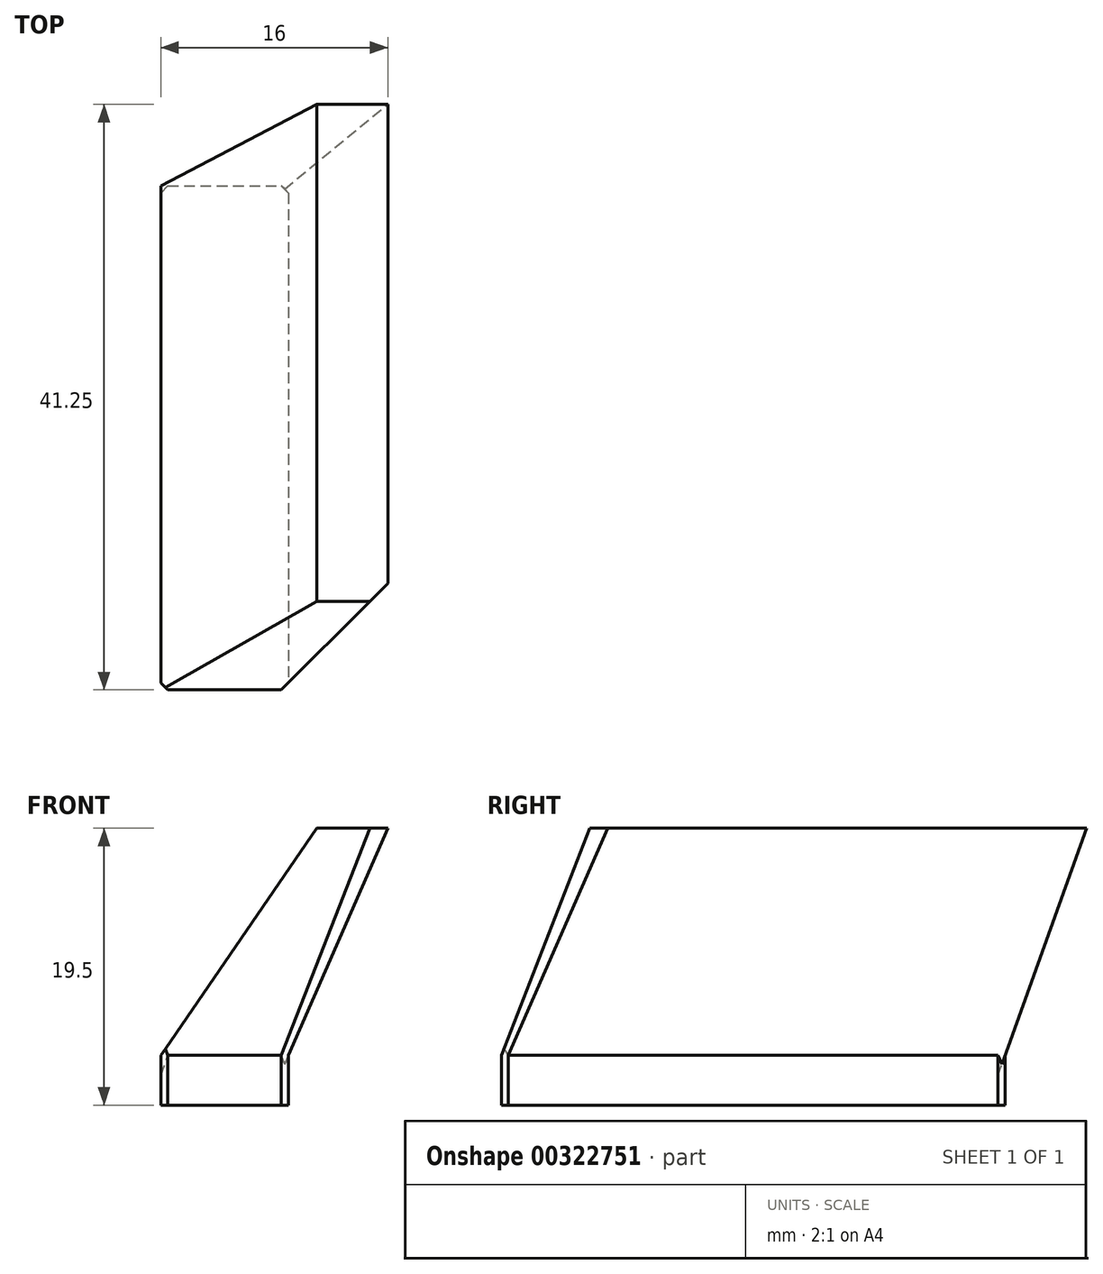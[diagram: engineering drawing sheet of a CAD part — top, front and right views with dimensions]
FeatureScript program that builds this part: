
annotation { "Feature Type Name" : "Feature", "Feature Type Description" : "" }
export const myFeature = defineFeature(function(context is Context, id is Id, definition is map)
    precondition{}
    {
        {
            assignVariable(context, id + "F0", {"variableType" : VariableType.LENGTH, "name" : "zoff", "lengthValue" : 16 * mm});
        }
        {
            var Q0;
            Q0=qCreatedBy(makeId("Top.planeOp"),FACE);
            var sketch = newSketch(context, id + "F1", { "sketchPlane" : qUnion([Q0])});
            skLineSegment(sketch, "E0.bottom", {"start": v(4.5, 17.75) * mm, "end": v(-4.5, 17.75) * mm});
            skLineSegment(sketch, "E0.top", {"start": v(4.5, -17.75) * mm, "end": v(-4.5, -17.75) * mm});
            skLineSegment(sketch, "E0.left", {"start": v(4.5, 17.75) * mm, "end": v(4.5, -17.75) * mm});
            skLineSegment(sketch, "E0.right", {"start": v(-4.5, 17.75) * mm, "end": v(-4.5, -17.75) * mm});
            skPoint(sketch, "E0.middle", {"position": v(0, 0) * mm});
            skSolve(sketch);
        }
        {
            var Q0;
            Q0=qCreatedBy(makeId("Top.planeOp"),FACE);
            cPlane(context, id + "F2", {"entities" : qUnion([Q0]), "cplaneType" : CPlaneType.OFFSET, "offset" : getVariable(context, 'zoff'), "oppositeDirection" : true, "width" : 150 * mm, "height" : 150 * mm});
        }
        {
            var Q0;
            Q0=qCreatedBy(id+"F2.planeOp",FACE);
            var sketch = newSketch(context, id + "F3", { "sketchPlane" : qUnion([Q0])});
            skLineSegment(sketch, "E1.bottom", {"start": v(-6.5, 23.5) * mm, "end": v(-11.5, 23.5) * mm});
            skLineSegment(sketch, "E1.top", {"start": v(-6.5, -11.5) * mm, "end": v(-11.5, -11.5) * mm});
            skLineSegment(sketch, "E1.left", {"start": v(-6.5, 23.5) * mm, "end": v(-6.5, -11.5) * mm});
            skLineSegment(sketch, "E1.right", {"start": v(-11.5, 23.5) * mm, "end": v(-11.5, -11.5) * mm});
            skPoint(sketch, "E1.middle", {"position": v(-9, 6) * mm});
            skSolve(sketch);
        }
        {
            var Q0;
            Q0=makeQuery(id+"F1.imprint","IMPRINT",FACE,{"disambiguationData":[TD([[makeQuery(id+"F1.imprint","IMPRINT",EDGE,{"derivedFrom":sQuery(id+"F1.wireOp",EDGE,"E0.bottom")}),1.0]])]});
            extrude(context, id + "F4", {"entities" : qUnion([Q0]), "depth" : 3.5 * mm, "offsetDistance" : 25 * mm});
        }
        {
            var Q0;
            Q0=makeQuery(id+"F4.opExtrude","CAP_FACE",FACE,{"disambiguationData":[OSD([sQuery(id+"F1.wireOp",EDGE,"E0.bottom"),sQuery(id+"F1.wireOp",EDGE,"E0.top"),sQuery(id+"F1.wireOp",EDGE,"E0.left"),sQuery(id+"F1.wireOp",EDGE,"E0.right")])],"isStart":true});
            var Q1;
            Q1=makeQuery(id+"F3.imprint","IMPRINT",FACE,{"disambiguationData":[TD([[makeQuery(id+"F3.imprint","IMPRINT",EDGE,{"derivedFrom":sQuery(id+"F3.wireOp",EDGE,"E1.bottom")}),1.0]])]});
            loft(context, id + "F5", {"operationType" : NewBodyOperationType.ADD, "sheetProfilesArray" : [{ "sheetProfileEntities" : qUnion([Q0]) }, { "sheetProfileEntities" : qUnion([Q1]) }]});
        }
        {
            var Q0;
            Q0=makeQuery(id+"F4.opExtrude","SWEPT_EDGE",EDGE,{"disambiguationData":[OSD([sQuery(id+"F1.wireOp",EDGE,"E0.bottom"),sQuery(id+"F1.wireOp",EDGE,"E0.left")])]});
            var Q1;
            Q1=makeQuery(id+"F4.opExtrude","SWEPT_EDGE",EDGE,{"disambiguationData":[OSD([sQuery(id+"F1.wireOp",EDGE,"E0.bottom"),sQuery(id+"F1.wireOp",EDGE,"E0.right")])]});
            var Q2;
            Q2=makeQuery(id+"F4.opExtrude","SWEPT_EDGE",EDGE,{"disambiguationData":[OSD([sQuery(id+"F1.wireOp",EDGE,"E0.top"),sQuery(id+"F1.wireOp",EDGE,"E0.right")])]});
            var Q3;
            Q3=makeQuery(id+"F4.opExtrude","SWEPT_EDGE",EDGE,{"disambiguationData":[OSD([sQuery(id+"F1.wireOp",EDGE,"E0.top"),sQuery(id+"F1.wireOp",EDGE,"E0.left")])]});
            chamfer(context, id + "F6", {"entities" : qUnion([Q0, Q1, Q2, Q3]), "width" : 0.5 * mm, "tangentPropagation" : true});
        }
        {
            var Q0;
            Q0=makeQuery(id+"F4.opExtrude","SWEPT_BODY",BODY,{"disambiguationData":[OSD([sQuery(id+"F1.wireOp",EDGE,"E0.bottom"),sQuery(id+"F1.wireOp",EDGE,"E0.top"),sQuery(id+"F1.wireOp",EDGE,"E0.left"),sQuery(id+"F1.wireOp",EDGE,"E0.right")])]});
            var Q1;
            Q1=makeQuery(id+"F4.opExtrude","CAP_EDGE",EDGE,{"disambiguationData":[OSD([sQuery(id+"F1.wireOp",EDGE,"E0.right")])],"isStart":false});
            transform(context, id + "F7", {"entities" : qUnion([Q0]), "transformType" : TransformType.ROTATION, "transformAxis" : qUnion([Q1]), "angle" : 180 * degree, "makeCopy" : false});
        }
    });
